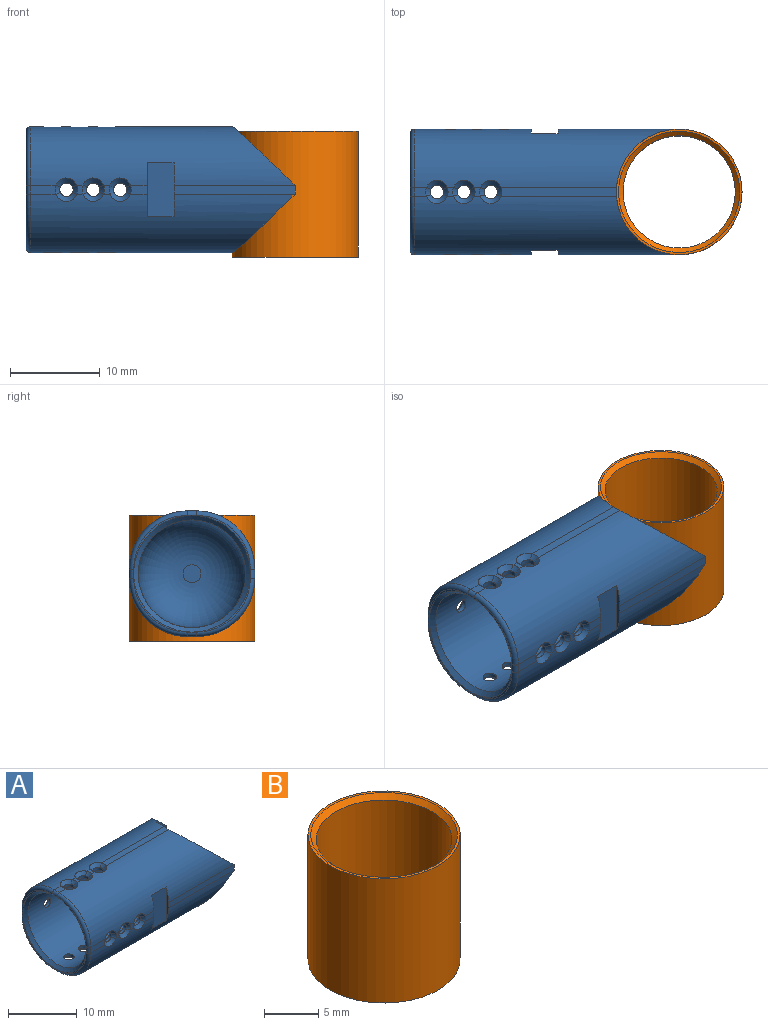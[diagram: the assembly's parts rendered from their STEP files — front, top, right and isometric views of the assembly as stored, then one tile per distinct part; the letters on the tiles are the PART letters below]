
ASSEMBLY  parts=2 mates=1
PART A: 105 faces, bbox 30x15.1x15.1 mm
  f0: plane 6.5x6.5mm, normal (-1,0,0), area 1.3mm2, adj f53,f54,f55,f56
  f1: plane 6.5x6.5mm, normal (-1,0,0), area 1.3mm2, adj f49,f51,f53,f56
  f2: plane 6.5x6.5mm, normal (-1,0,0), area 1.3mm2, adj f48,f49,f50,f56
  f3: plane 1.85x1mm, normal (0,-1,0), area 1.8mm2, adj f39,f46,f47,f82
  f4: plane 1x0.71mm, normal (0,-1,0), area 0.6mm2, adj f46,f47,f83,f86
  f5: plane 1x0.71mm, normal (0,-1,0), area 0.6mm2, adj f46,f47,f87,f90
  f6: plane 1.35x1mm, normal (0,0,-1), area 1.3mm2, adj f45,f47,f49,f78
  f7: plane 1x0.71mm, normal (0,0,-1), area 0.6mm2, adj f45,f47,f74,f79
  f8: plane 1x0.71mm, normal (0,0,-1), area 0.6mm2, adj f45,f47,f71,f75
  f9: plane 2.85x1mm, normal (0,1,0), area 2.8mm2, adj f44,f45,f50,f66
  f10: plane 1x0.71mm, normal (0,1,0), area 0.6mm2, adj f44,f45,f62,f67
  f11: plane 1x0.71mm, normal (0,1,0), area 0.6mm2, adj f44,f45,f58,f63
  f12: plane 12.87x1mm, normal (0,0,1), area 12.8mm2, adj f22,f44,f46,f99
  f13: plane 1x0.71mm, normal (0,0,1), area 0.6mm2, adj f44,f46,f98,f102
  f14: plane 1x0.71mm, normal (0,0,1), area 0.6mm2, adj f44,f46,f94,f103
  f15: plane 1.85x1mm, normal (0,1,0), area 1.8mm2, adj f42,f44,f45,f59
  f16: plane 1.35x1mm, normal (0,0,1), area 1.3mm2, adj f44,f46,f54,f95
  f17: plane 13.5x1mm, normal (0,-1,0), area 13.5mm2, adj f22,f38,f46,f47
  f18: plane 13.5x1mm, normal (0,1,0), area 13.5mm2, adj f22,f41,f44,f45
  f19: plane 6.5x6.5mm, normal (-1,0,0), area 1.3mm2, adj f50,f52,f54,f56
  f20: plane 2.85x1mm, normal (0,-1,0), area 2.8mm2, adj f46,f47,f53,f91
  f21: plane 12.87x1mm, normal (0,0,-1), area 12.8mm2, adj f22,f45,f47,f70
  f22: cylinder r=7mm len=14mm, axis (0,0,1), area 208mm2, adj f12,f17,f18,f21,f44,f45,f46,f47
  f23: cylinder r=6mm len=14.5mm, axis (-1,0,0), area 525.4mm2, adj f25,f26,f27,f28,f29,f30,f31,f32
  f24: plane 2x2mm, normal (-1,0,0), area 3.1mm2, adj f25
  f25: torus R=1mm, axis (-1,0,0), area 206.4mm2, adj f23,f24
  f26: cylinder r=0.75mm len=1.5mm, axis (0,0,1), area 2.4mm2, adj f23,f73,f74,f75,f76
  f27: cylinder r=0.75mm len=1.5mm, axis (0,0,1), area 2.4mm2, adj f23,f101,f102,f103,f104
  f28: cylinder r=0.75mm len=1.5mm, axis (0,0,1), area 2.4mm2, adj f23,f69,f70,f71,f72
  f29: cylinder r=0.75mm len=1.5mm, axis (0,0,1), area 2.4mm2, adj f23,f97,f98,f99,f100
  f30: cylinder r=0.75mm len=1.5mm, axis (0,0,1), area 2.4mm2, adj f23,f77,f78,f79,f80
  f31: cylinder r=0.75mm len=1.5mm, axis (0,0,1), area 2.4mm2, adj f23,f93,f94,f95,f96
  f32: cylinder r=0.75mm len=1.5mm, axis (0,-1,0), area 2.5mm2, adj f23,f85,f86,f87,f88
  f33: cylinder r=0.75mm len=1.5mm, axis (0,-1,0), area 2.5mm2, adj f23,f61,f62,f63,f64
  f34: cylinder r=0.75mm len=1.5mm, axis (0,-1,0), area 2.5mm2, adj f23,f89,f90,f91,f92
  f35: cylinder r=0.75mm len=1.5mm, axis (0,-1,0), area 2.5mm2, adj f23,f65,f66,f67,f68
  f36: cylinder r=0.75mm len=1.5mm, axis (0,-1,0), area 2.5mm2, adj f23,f81,f82,f83,f84
  f37: cylinder r=0.75mm len=1.5mm, axis (0,-1,0), area 2.5mm2, adj f23,f57,f58,f59,f60
  f38: plane 6x0.5mm, normal (-1,0,0), area 2.2mm2, adj f17,f40,f46,f47
  f39: plane 6x0.5mm, normal (1,0,0), area 2.2mm2, adj f3,f40,f46,f47
  f40: plane 6x3mm, normal (0,-1,0), area 18mm2, adj f38,f39,f46,f47
  f41: plane 6x0.5mm, normal (-1,0,0), area 2.2mm2, adj f18,f43,f44,f45
  f42: plane 6x0.5mm, normal (1,0,0), area 2.2mm2, adj f15,f43,f44,f45
  f43: plane 6x3mm, normal (0,1,0), area 18mm2, adj f41,f42,f44,f45
  f44: cylinder r=6.5mm len=29.5mm, axis (1,0,0), area 241mm2, adj f9,f10,f11,f12,f13,f14,f15,f16
  f45: cylinder r=6.5mm len=29.5mm, axis (-1,0,0), area 241mm2, adj f6,f7,f8,f9,f10,f11,f15,f18
  f46: cylinder r=6.5mm len=29.5mm, axis (-1,0,0), area 241mm2, adj f3,f4,f5,f12,f13,f14,f16,f17
  f47: cylinder r=6.5mm len=29.5mm, axis (1,0,0), area 241mm2, adj f3,f4,f5,f6,f7,f8,f17,f20
  f48: torus R=6mm, axis (1,0,0), area 7.8mm2, adj f2,f45,f49,f50
  f49: cylinder r=0.5mm len=1mm, axis (0,-1,0), area 0.8mm2, adj f1,f2,f6,f48,f51
  f50: cylinder r=0.5mm len=1mm, axis (0,0,-1), area 0.8mm2, adj f2,f9,f19,f48,f52
  f51: torus R=6mm, axis (1,0,0), area 7.8mm2, adj f1,f47,f49,f53
  f52: torus R=6mm, axis (1,0,0), area 7.8mm2, adj f19,f44,f50,f54
  f53: cylinder r=0.5mm len=1mm, axis (0,0,1), area 0.8mm2, adj f0,f1,f20,f51,f55
  f54: cylinder r=0.5mm len=1mm, axis (0,1,0), area 0.8mm2, adj f0,f16,f19,f52,f55
  f55: torus R=6mm, axis (1,0,0), area 7.8mm2, adj f0,f46,f53,f54
  f56: cone r=6mm half-angle=45deg, axis (-1,0,0), area 27.8mm2, adj f0,f1,f2,f19,f23
  f57: bspline ~2.29x1.01mm, area 1.7mm2, adj f37,f45,f58,f59
  f58: cone r=1.25mm half-angle=45deg, axis (0,1,0), area 0.6mm2, adj f11,f37,f57,f60
  f59: cone r=1.25mm half-angle=45deg, axis (0,1,0), area 0.6mm2, adj f15,f37,f57,f60
  f60: bspline ~2.29x1.01mm, area 1.7mm2, adj f37,f44,f58,f59
  f61: bspline ~2.29x1.01mm, area 1.7mm2, adj f33,f45,f62,f63
  f62: cone r=1.25mm half-angle=45deg, axis (0,1,0), area 0.6mm2, adj f10,f33,f61,f64
  f63: cone r=1.25mm half-angle=45deg, axis (0,1,0), area 0.6mm2, adj f11,f33,f61,f64
  f64: bspline ~2.29x1.01mm, area 1.7mm2, adj f33,f44,f62,f63
  f65: bspline ~2.29x1.01mm, area 1.7mm2, adj f35,f45,f66,f67
  f66: cone r=1.25mm half-angle=45deg, axis (0,1,0), area 0.6mm2, adj f9,f35,f65,f68
  f67: cone r=1.25mm half-angle=45deg, axis (0,1,0), area 0.6mm2, adj f10,f35,f65,f68
  f68: bspline ~2.29x1.01mm, area 1.7mm2, adj f35,f44,f66,f67
  f69: bspline ~2.29x1.01mm, area 1.7mm2, adj f28,f45,f70,f71
  f70: cone r=1.25mm half-angle=45deg, axis (0,0,-1), area 0.6mm2, adj f21,f28,f69,f72
  f71: cone r=1.25mm half-angle=45deg, axis (0,0,-1), area 0.6mm2, adj f8,f28,f69,f72
  f72: bspline ~2.29x1.01mm, area 1.7mm2, adj f28,f47,f70,f71
  f73: bspline ~2.29x1.01mm, area 1.7mm2, adj f26,f47,f74,f75
  f74: cone r=1.25mm half-angle=45deg, axis (0,0,-1), area 0.6mm2, adj f7,f26,f73,f76
  f75: cone r=1.25mm half-angle=45deg, axis (0,0,-1), area 0.6mm2, adj f8,f26,f73,f76
  f76: bspline ~2.29x1.01mm, area 1.7mm2, adj f26,f45,f74,f75
  f77: bspline ~2.29x1.01mm, area 1.7mm2, adj f30,f47,f78,f79
  f78: cone r=1.25mm half-angle=45deg, axis (0,0,-1), area 0.6mm2, adj f6,f30,f77,f80
  f79: cone r=1.25mm half-angle=45deg, axis (0,0,-1), area 0.6mm2, adj f7,f30,f77,f80
  f80: bspline ~2.29x1.01mm, area 1.7mm2, adj f30,f45,f78,f79
  f81: bspline ~2.29x1.01mm, area 1.7mm2, adj f36,f47,f82,f83
  f82: cone r=0.75mm half-angle=45deg, axis (0,-1,0), area 0.6mm2, adj f3,f36,f81,f84
  f83: cone r=0.75mm half-angle=45deg, axis (0,-1,0), area 0.6mm2, adj f4,f36,f81,f84
  f84: bspline ~2.29x1.01mm, area 1.7mm2, adj f36,f46,f82,f83
  f85: bspline ~2.29x1.01mm, area 1.7mm2, adj f32,f47,f86,f87
  f86: cone r=0.75mm half-angle=45deg, axis (0,-1,0), area 0.6mm2, adj f4,f32,f85,f88
  f87: cone r=0.75mm half-angle=45deg, axis (0,-1,0), area 0.6mm2, adj f5,f32,f85,f88
  f88: bspline ~2.29x1.01mm, area 1.7mm2, adj f32,f46,f86,f87
  f89: bspline ~2.29x1.01mm, area 1.7mm2, adj f34,f47,f90,f91
  f90: cone r=0.75mm half-angle=45deg, axis (0,-1,0), area 0.6mm2, adj f5,f34,f89,f92
  f91: cone r=0.75mm half-angle=45deg, axis (0,-1,0), area 0.6mm2, adj f20,f34,f89,f92
  f92: bspline ~2.29x1.01mm, area 1.7mm2, adj f34,f46,f90,f91
  f93: bspline ~2.29x1.01mm, area 1.7mm2, adj f31,f46,f94,f95
  f94: cone r=0.75mm half-angle=45deg, axis (0,0,1), area 0.6mm2, adj f14,f31,f93,f96
  f95: cone r=0.75mm half-angle=45deg, axis (0,0,1), area 0.6mm2, adj f16,f31,f93,f96
  f96: bspline ~2.29x1.01mm, area 1.7mm2, adj f31,f44,f94,f95
  f97: bspline ~2.29x1.01mm, area 1.7mm2, adj f29,f44,f98,f99
  f98: cone r=0.75mm half-angle=45deg, axis (0,0,1), area 0.6mm2, adj f13,f29,f97,f100
  f99: cone r=0.75mm half-angle=45deg, axis (0,0,1), area 0.6mm2, adj f12,f29,f97,f100
  f100: bspline ~2.29x1.01mm, area 1.7mm2, adj f29,f46,f98,f99
  f101: bspline ~2.29x1.01mm, area 1.7mm2, adj f27,f46,f102,f103
  f102: cone r=0.75mm half-angle=45deg, axis (0,0,1), area 0.6mm2, adj f13,f27,f101,f104
  f103: cone r=0.75mm half-angle=45deg, axis (0,0,1), area 0.6mm2, adj f14,f27,f101,f104
  f104: bspline ~2.29x1.01mm, area 1.7mm2, adj f27,f44,f102,f103
PART B: 6 faces, bbox 14x14x14 mm
  f0: cylinder r=6.25mm len=13mm, axis (0,0,-1), area 510.5mm2, adj f4,f5
  f1: cylinder r=7mm len=14mm, axis (0,0,-1), area 615.8mm2, adj f2,f3
  f2: plane 14x14mm, normal (0,0,1), area 10.8mm2, adj f1,f4
  f3: plane 14x14mm, normal (0,0,-1), area 10.8mm2, adj f1,f5
  f4: cone r=6.25mm half-angle=45deg, axis (0,0,1), area 28.9mm2, adj f0,f2
  f5: cone r=6.75mm half-angle=45deg, axis (0,0,-1), area 28.9mm2, adj f0,f3
PLACE A t=(14.12,-2.86,5.31)mm
PLACE B t=(-37.52,-40.2,4.81)mm
MATE fastened B.f0 <-> A.f22  axis (0,0,-1) through (29.12,-2.86,5.31)mm
